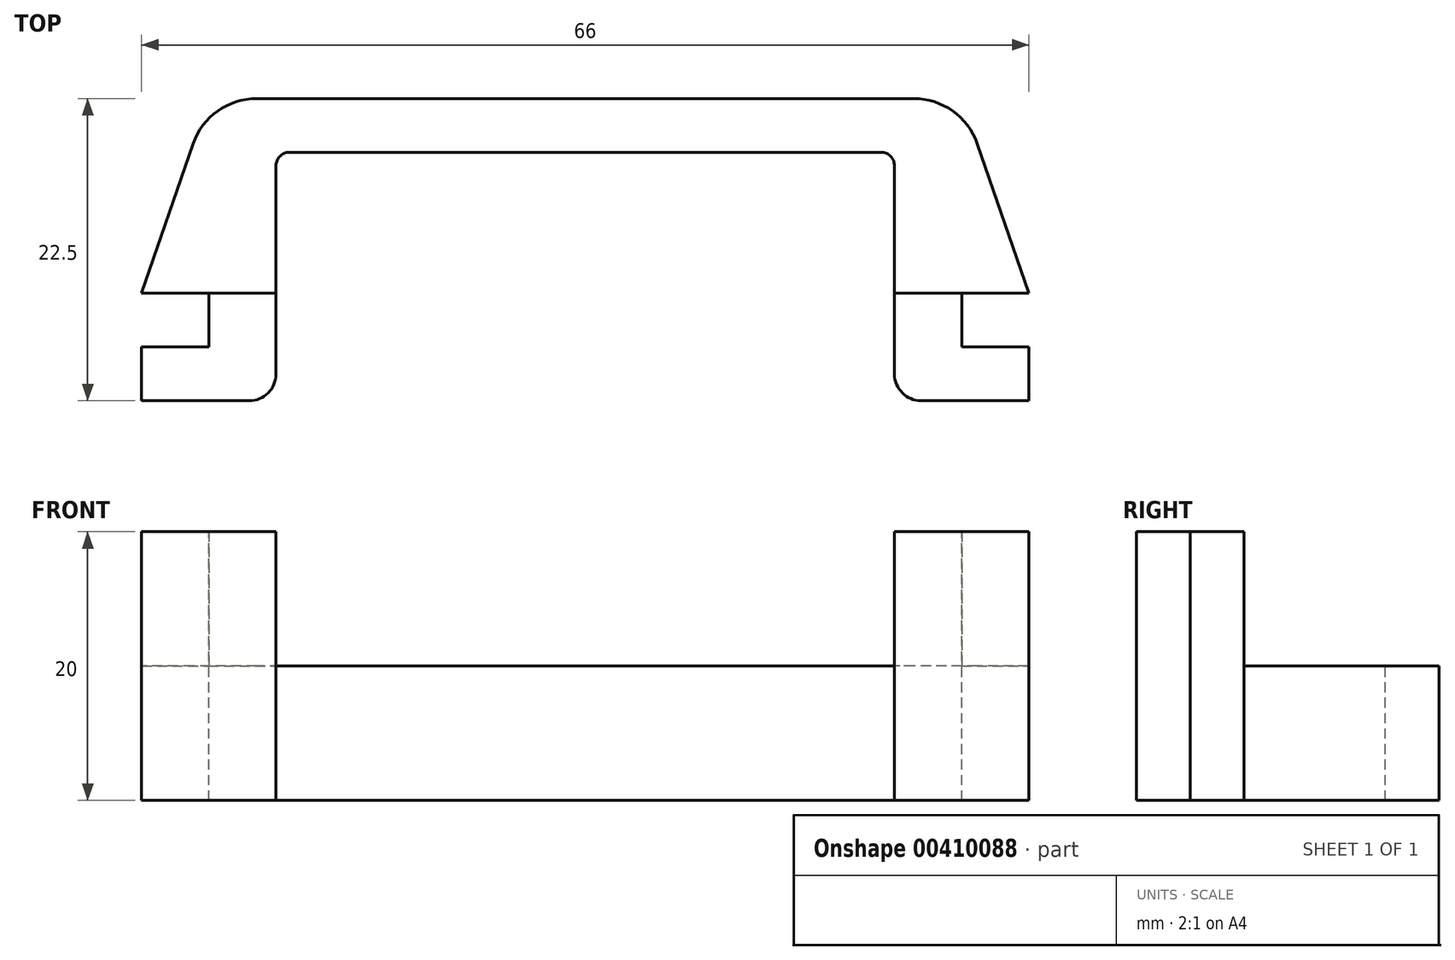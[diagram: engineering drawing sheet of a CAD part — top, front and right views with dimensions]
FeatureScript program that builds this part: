
annotation { "Feature Type Name" : "Feature", "Feature Type Description" : "" }
export const myFeature = defineFeature(function(context is Context, id is Id, definition is map)
    precondition{}
    {
        {
            var Q0;
            Q0=qCreatedBy(makeId("Top.planeOp"),FACE);
            var sketch = newSketch(context, id + "F0", { "sketchPlane" : qUnion([Q0])});
            skLineSegment(sketch, "E0", {"start": v(-33.73, -19.4) * mm, "end": v(-25.73, -19.4) * mm});
            skLineSegment(sketch, "E1", {"start": v(-23.73, -17.4) * mm, "end": v(-23.73, -1.9) * mm});
            skLineSegment(sketch, "E2", {"start": v(-22.73, -0.9) * mm, "end": v(21.27, -0.9) * mm});
            skLineSegment(sketch, "E3", {"start": v(22.27, -1.9) * mm, "end": v(22.27, -17.4) * mm});
            skLineSegment(sketch, "E4", {"start": v(24.27, -19.4) * mm, "end": v(32.27, -19.4) * mm});
            skLineSegment(sketch, "E5", {"start": v(32.27, -19.4) * mm, "end": v(32.27, -15.4) * mm});
            skLineSegment(sketch, "E6", {"start": v(32.27, -15.4) * mm, "end": v(27.27, -15.4) * mm});
            skLineSegment(sketch, "E7", {"start": v(27.27, -15.4) * mm, "end": v(27.27, -11.4) * mm});
            skLineSegment(sketch, "E8", {"start": v(27.27, -11.4) * mm, "end": v(32.27, -11.4) * mm});
            skLineSegment(sketch, "E9", {"start": v(32.27, -11.4) * mm, "end": v(28.43, -0.26) * mm});
            skLineSegment(sketch, "E10", {"start": v(23.7, 3.1) * mm, "end": v(-25.16, 3.1) * mm});
            skLineSegment(sketch, "E11", {"start": v(-29.9, -0.26) * mm, "end": v(-33.73, -11.4) * mm});
            skLineSegment(sketch, "E12", {"start": v(-33.73, -11.4) * mm, "end": v(-28.73, -11.4) * mm});
            skLineSegment(sketch, "E13", {"start": v(-28.73, -11.4) * mm, "end": v(-28.73, -15.4) * mm});
            skLineSegment(sketch, "E14", {"start": v(-28.73, -15.4) * mm, "end": v(-33.73, -15.4) * mm});
            skLineSegment(sketch, "E15", {"start": v(-33.73, -15.4) * mm, "end": v(-33.73, -19.4) * mm});
            skPoint(sketch, "E16.visualSharp", {"position": v(-28.73, 3.1) * mm});
            skArc(sketch, "E16.filletArc", {"start": v(-25.16, 3.1) * mm, "mid": v(-28.07, 2.18) * mm, "end": v(-29.9, -0.26) * mm});
            skPoint(sketch, "E17.visualSharp", {"position": v(-23.73, -0.9) * mm});
            skArc(sketch, "E17.filletArc", {"start": v(-22.73, -0.9) * mm, "mid": v(-23.44, -1.18) * mm, "end": v(-23.73, -1.9) * mm});
            skPoint(sketch, "E18.visualSharp", {"position": v(22.27, -0.9) * mm});
            skArc(sketch, "E18.filletArc", {"start": v(22.27, -1.9) * mm, "mid": v(21.98, -1.18) * mm, "end": v(21.27, -0.9) * mm});
            skPoint(sketch, "E19.visualSharp", {"position": v(27.27, 3.1) * mm});
            skArc(sketch, "E19.filletArc", {"start": v(28.43, -0.26) * mm, "mid": v(26.6, 2.18) * mm, "end": v(23.7, 3.1) * mm});
            skPoint(sketch, "E20.visualSharp", {"position": v(22.27, -19.4) * mm});
            skArc(sketch, "E20.filletArc", {"start": v(22.27, -17.4) * mm, "mid": v(22.86, -18.8) * mm, "end": v(24.27, -19.4) * mm});
            skPoint(sketch, "E21.visualSharp", {"position": v(-23.73, -19.4) * mm});
            skArc(sketch, "E21.filletArc", {"start": v(-25.73, -19.4) * mm, "mid": v(-24.32, -18.8) * mm, "end": v(-23.73, -17.4) * mm});
            skLineSegment(sketch, "E22", {"start": v(-28.73, -11.4) * mm, "end": v(-23.73, -11.4) * mm});
            skLineSegment(sketch, "E23", {"start": v(27.27, -11.4) * mm, "end": v(22.27, -11.4) * mm});
            skSolve(sketch);
        }
        {
            var Q0;
            Q0=makeQuery(id+"F0.imprint","IMPRINT",FACE,{"disambiguationData":[TD([[makeQuery(id+"F0.imprint","IMPRINT",EDGE,{"derivedFrom":sQuery(id+"F0.wireOp",EDGE,"E0")}),1.0]])]});
            var Q1;
            Q1=makeQuery(id+"F0.imprint","IMPRINT",FACE,{"disambiguationData":[TD([[makeQuery(id+"F0.imprint","IMPRINT",EDGE,{"derivedFrom":sQuery(id+"F0.wireOp",EDGE,"E2")}),1.0]])]});
            var Q2;
            Q2=makeQuery(id+"F0.imprint","IMPRINT",FACE,{"disambiguationData":[TD([[makeQuery(id+"F0.imprint","IMPRINT",EDGE,{"derivedFrom":sQuery(id+"F0.wireOp",EDGE,"E4")}),1.0]])]});
            extrude(context, id + "F1", {"entities" : qUnion([Q0, Q1, Q2]), "oppositeDirection" : true, "depth" : 10 * mm});
        }
        {
            var Q0;
            Q0=makeQuery(id+"F0.imprint","IMPRINT",FACE,{"disambiguationData":[TD([[makeQuery(id+"F0.imprint","IMPRINT",EDGE,{"derivedFrom":sQuery(id+"F0.wireOp",EDGE,"E0")}),1.0]])]});
            var Q1;
            Q1=makeQuery(id+"F0.imprint","IMPRINT",FACE,{"disambiguationData":[TD([[makeQuery(id+"F0.imprint","IMPRINT",EDGE,{"derivedFrom":sQuery(id+"F0.wireOp",EDGE,"E4")}),1.0]])]});
            extrude(context, id + "F2", {"entities" : qUnion([Q0, Q1]), "operationType" : NewBodyOperationType.ADD, "depth" : 10 * mm});
        }
    });
